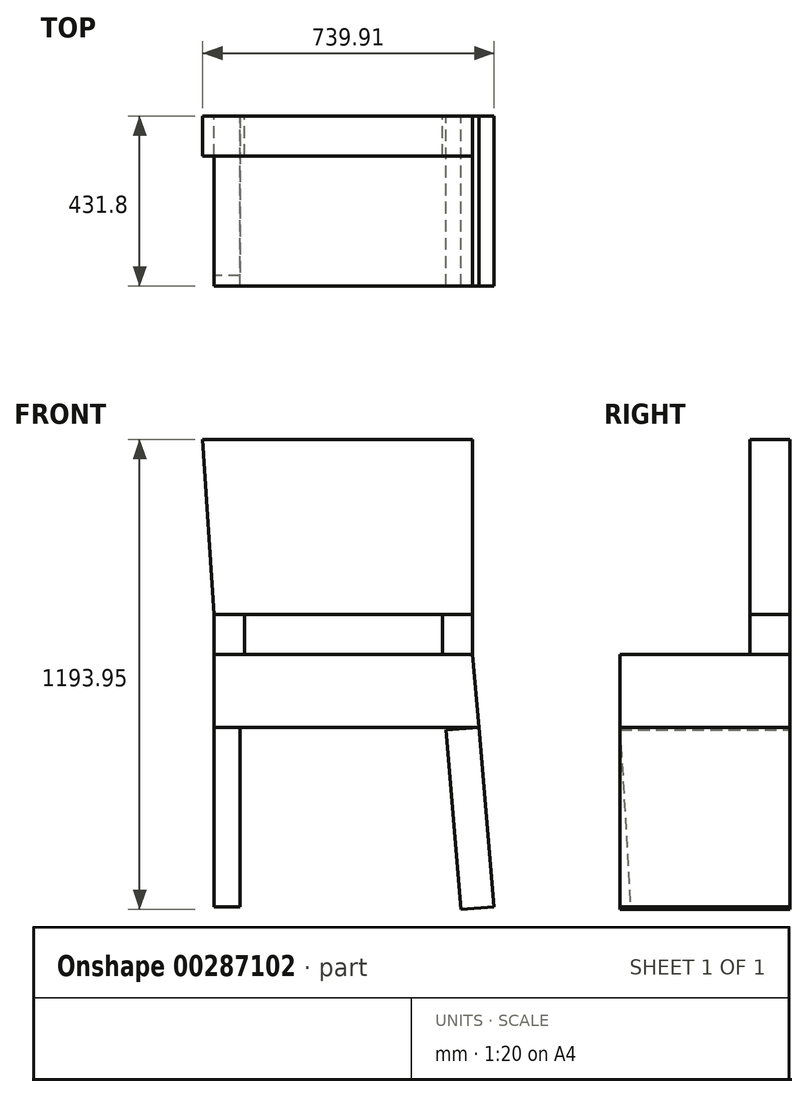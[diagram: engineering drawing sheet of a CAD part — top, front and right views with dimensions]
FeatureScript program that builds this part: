
annotation { "Feature Type Name" : "Feature", "Feature Type Description" : "" }
export const myFeature = defineFeature(function(context is Context, id is Id, definition is map)
    precondition{}
    {
        {
            var Q0;
            Q0=qCreatedBy(makeId("Front.planeOp"),FACE);
            var sketch = newSketch(context, id + "F0", { "sketchPlane" : qUnion([Q0])});
            skPoint(sketch, "E0.middle", {"position": v(0, 308.16) * mm});
            skLineSegment(sketch, "E1", {"start": v(-371.6, 526.13) * mm, "end": v(285.02, 526.13) * mm});
            skLineSegment(sketch, "E2", {"start": v(-371.6, 627.73) * mm, "end": v(285.02, 627.73) * mm});
            skLineSegment(sketch, "E3", {"start": v(285.02, 627.73) * mm, "end": v(285.02, 1072.77) * mm});
            skLineSegment(sketch, "E4", {"start": v(285.02, 1072.77) * mm, "end": v(-400.78, 1072.77) * mm});
            skLineSegment(sketch, "E5", {"start": v(-400.78, 1072.77) * mm, "end": v(-371.6, 627.73) * mm});
            skLineSegment(sketch, "E6", {"start": v(-371.6, 627.73) * mm, "end": v(-371.6, 526.13) * mm});
            skLineSegment(sketch, "E7", {"start": v(-294.32, 627.73) * mm, "end": v(-294.32, 526.13) * mm});
            skLineSegment(sketch, "E8", {"start": v(285.02, 627.73) * mm, "end": v(285.02, 526.13) * mm});
            skLineSegment(sketch, "E9", {"start": v(208.09, 627.73) * mm, "end": v(208.09, 526.13) * mm});
            skLineSegment(sketch, "E10", {"start": v(-371.6, 526.13) * mm, "end": v(-371.6, 341.45) * mm});
            skLineSegment(sketch, "E11", {"start": v(-371.6, 341.45) * mm, "end": v(300.63, 341.45) * mm});
            skLineSegment(sketch, "E12", {"start": v(300.63, 341.45) * mm, "end": v(285.02, 526.13) * mm});
            skSolve(sketch);
        }
        {
            var Q0;
            {var subQ0=sQuery(id+"F0.wireOp",EDGE,"E10");Q0=makeQuery(id+"F0.imprint","IMPRINT",FACE,{"disambiguationData":[TD([[makeQuery(id+"F0.imprint","IMPRINT",EDGE,{"derivedFrom":subQ0}),1.0]])]});}
            extrude(context, id + "F1", {"entities" : qUnion([Q0]), "depth" : 431.8 * mm});
        }
        {
            var Q0;
            {var subQ0=sQuery(id+"F0.wireOp",EDGE,"E6");Q0=makeQuery(id+"F0.imprint","IMPRINT",FACE,{"disambiguationData":[TD([[makeQuery(id+"F0.imprint","IMPRINT",EDGE,{"derivedFrom":subQ0}),1.0]])]});}
            var Q1;
            {var subQ0=sQuery(id+"F0.wireOp",EDGE,"E8");Q1=makeQuery(id+"F0.imprint","IMPRINT",FACE,{"disambiguationData":[TD([[makeQuery(id+"F0.imprint","IMPRINT",EDGE,{"derivedFrom":subQ0}),-1.0]])]});}
            extrude(context, id + "F2", {"entities" : qUnion([Q0, Q1]), "depth" : 101.6 * mm});
        }
        {
            var Q0;
            {var subQ0=sQuery(id+"F0.wireOp",EDGE,"E3");Q0=makeQuery(id+"F0.imprint","IMPRINT",FACE,{"disambiguationData":[TD([[makeQuery(id+"F0.imprint","IMPRINT",EDGE,{"derivedFrom":subQ0}),1.0]])]});}
            extrude(context, id + "F3", {"entities" : qUnion([Q0]), "depth" : 101.6 * mm});
        }
        {
            var Q0;
            Q0=makeQuery(id+"F1.opExtrude","SWEPT_FACE",FACE,{"disambiguationData":[OSD([sQuery(id+"F0.wireOp",EDGE,"E10")])]});
            var sketch = newSketch(context, id + "F4", { "sketchPlane" : qUnion([Q0])});
            skLineSegment(sketch, "E13", {"start": v(0, 341.45) * mm, "end": v(0, -114.97) * mm});
            skLineSegment(sketch, "E14", {"start": v(0, -114.97) * mm, "end": v(405.07, -114.97) * mm});
            skLineSegment(sketch, "E15", {"start": v(431.8, 341.45) * mm, "end": v(405.07, -114.97) * mm});
            skSolve(sketch);
        }
        {
            var Q0;
            Q0=makeQuery(id+"F4.imprint","IMPRINT",FACE,{"disambiguationData":[TD([[makeQuery(id+"F4.imprint","IMPRINT",EDGE,{"derivedFrom":sQuery(id+"F4.wireOp",EDGE,"E13")}),1.0]])]});
            extrude(context, id + "F5", {"entities" : qUnion([Q0]), "operationType" : NewBodyOperationType.ADD, "oppositeDirection" : true, "depth" : 66.04 * mm});
        }
        {
            var Q0;
            Q0=makeQuery(id+"F1.opExtrude","SWEPT_FACE",FACE,{"disambiguationData":[OSD([sQuery(id+"F0.wireOp",EDGE,"E12")])]});
            var sketch = newSketch(context, id + "F6", { "sketchPlane" : qUnion([Q0])});
            skLineSegment(sketch, "E16", {"start": v(-431.8, 314.92) * mm, "end": v(-431.8, -142.28) * mm});
            skLineSegment(sketch, "E17", {"start": v(-431.8, -142.28) * mm, "end": v(0, -142.28) * mm});
            skLineSegment(sketch, "E18", {"start": v(0, -142.28) * mm, "end": v(0, 314.92) * mm});
            skSolve(sketch);
        }
        {
            var Q0;
            Q0=makeQuery(id+"F6.imprint","IMPRINT",FACE,{"disambiguationData":[TD([[makeQuery(id+"F6.imprint","IMPRINT",EDGE,{"derivedFrom":sQuery(id+"F6.wireOp",EDGE,"E16")}),1.0]])]});
            extrude(context, id + "F7", {"entities" : qUnion([Q0]), "oppositeDirection" : true, "depth" : 83.82 * mm});
        }
    });
